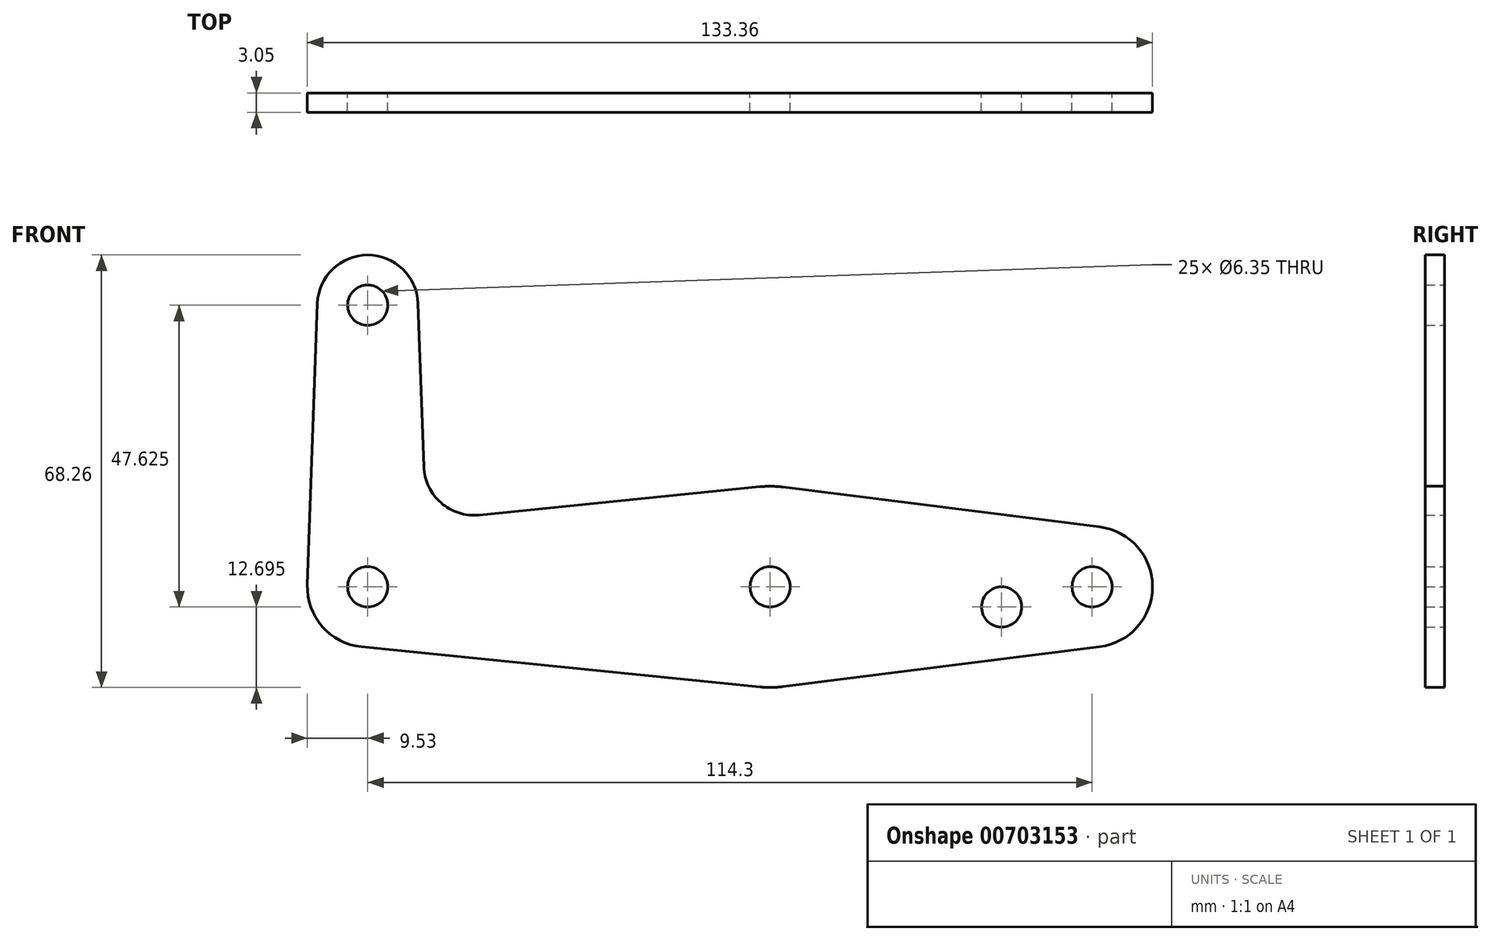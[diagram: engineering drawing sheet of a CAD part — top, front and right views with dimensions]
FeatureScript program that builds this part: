
annotation { "Feature Type Name" : "Feature", "Feature Type Description" : "" }
export const myFeature = defineFeature(function(context is Context, id is Id, definition is map)
    precondition{}
    {
        {
            var Q0;
            Q0=qCreatedBy(makeId("Front.planeOp"),FACE);
            var sketch = newSketch(context, id + "F0", { "sketchPlane" : qUnion([Q0])});
            skLineSegment(sketch, "E0", {"start": v(114.3, 0) * mm, "end": v(0, 0) * mm});
            skLineSegment(sketch, "E1", {"start": v(0, 0) * mm, "end": v(0, 44.45) * mm});
            skCircle(sketch, "E2", {"center": v(0, 44.45) * mm, "radius": 7.94 * mm});
            skCircle(sketch, "E3", {"center": v(0, 0) * mm, "radius": 9.53 * mm});
            skCircle(sketch, "E4", {"center": v(63.5, 0) * mm, "radius": 15.88 * mm});
            skCircle(sketch, "E5", {"center": v(114.3, 0) * mm, "radius": 9.53 * mm});
            skLineSegment(sketch, "E6", {"start": v(8.85, 18.97) * mm, "end": v(7.93, 44.73) * mm});
            skLineSegment(sketch, "E7", {"start": v(-9.52, 0.34) * mm, "end": v(-7.93, 44.73) * mm});
            skLineSegment(sketch, "E8", {"start": v(17.6, 11.34) * mm, "end": v(61.91, 15.8) * mm});
            skLineSegment(sketch, "E9", {"start": v(-0.95, -9.48) * mm, "end": v(61.91, -15.8) * mm});
            skLineSegment(sketch, "E10", {"start": v(65.48, -15.75) * mm, "end": v(115.5, -9.45) * mm});
            skLineSegment(sketch, "E11", {"start": v(65.48, 15.75) * mm, "end": v(115.5, 9.45) * mm});
            skCircle(sketch, "E12", {"center": v(0, 44.45) * mm, "radius": 3.18 * mm});
            skCircle(sketch, "E13", {"center": v(0, 0) * mm, "radius": 3.18 * mm});
            skCircle(sketch, "E14", {"center": v(63.5, 0) * mm, "radius": 3.18 * mm});
            skCircle(sketch, "E15", {"center": v(114.3, 0) * mm, "radius": 3.18 * mm});
            skArc(sketch, "E16.filletArc", {"start": v(8.85, 18.97) * mm, "mid": v(11.57, 13.26) * mm, "end": v(17.6, 11.34) * mm});
            skCircle(sketch, "E17", {"center": v(100.03, -3.17) * mm, "radius": 3.18 * mm});
            skSolve(sketch);
        }
        {
            var Q0;
            Q0 = qSketchRegion(id + "F0", true);
            var Q1;
            {var subQ0=sQuery(id+"F0.wireOp",EDGE,"E3");var subQ1=sQuery(id+"F0.wireOp",EDGE,"E0");var subQ2=makeQuery(id+"F0.imprint","INTERSECT",VERTEX,{"derivedFrom":[subQ1,subQ0]});Q1=makeQuery(id+"F0.imprint","IMPRINT",FACE,{"disambiguationData":[TD([[makeQuery(id+"F0.imprint","IMPRINT",EDGE,{"disambiguationData":[TD([[subQ2,-1.0]])],"derivedFrom":subQ1}),-1.0]])]});}
            extrude(context, id + "F1", {"entities" : qUnion([Q0, Q1]), "depth" : 3.05 * mm, "offsetDistance" : 25.4 * mm});
        }
    });
